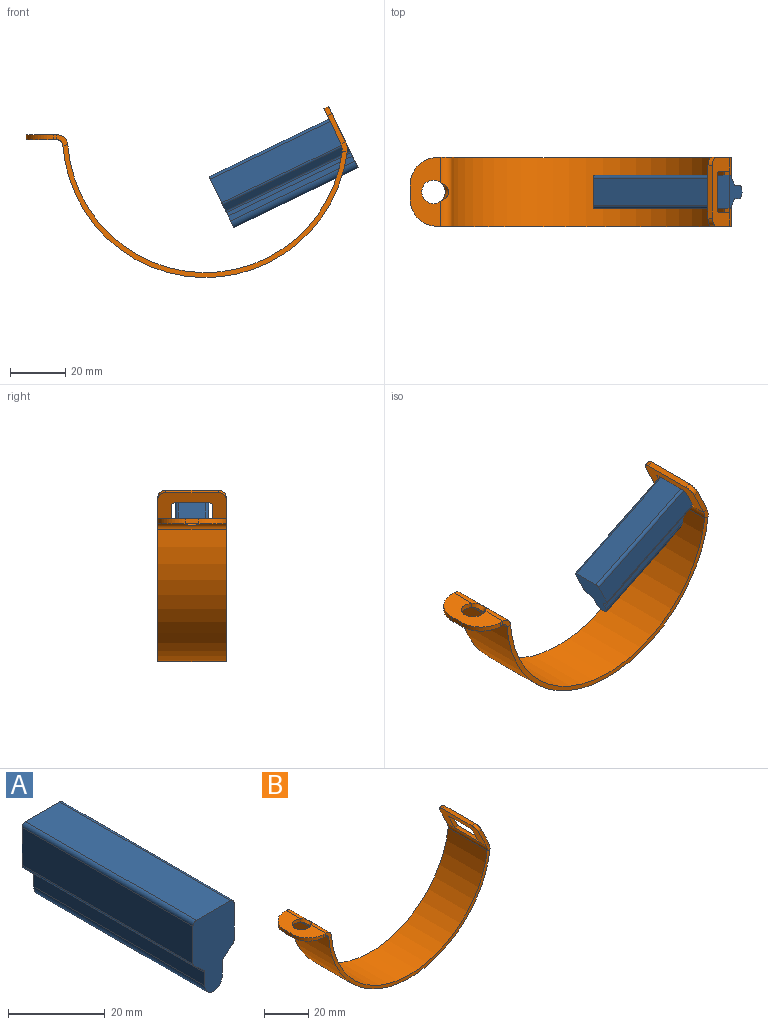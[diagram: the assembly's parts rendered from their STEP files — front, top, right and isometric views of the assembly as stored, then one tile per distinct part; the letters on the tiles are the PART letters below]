
ASSEMBLY  parts=2 mates=1
PART A: 17 faces, bbox 12x50x20.5 mm
  f0: plane 50x2.81mm, normal (-0.65,0,-0.76), area 184.7mm2, adj f9,f10,f11,f16
  f1: plane 50x3.34mm, normal (-1,0,0), area 167.1mm2, adj f2,f9,f10,f11
  f2: cylinder r=2.5mm len=50mm, axis (0,1,0), area 409.1mm2, adj f1,f3,f9,f10
  f3: plane 50x2.09mm, normal (1,0,0), area 104.6mm2, adj f2,f4,f9,f10
  f4: plane 50x1.32mm, normal (1,0,0), area 65.8mm2, adj f3,f9,f10,f12
  f5: plane 50x2.81mm, normal (0.65,0,-0.76), area 184.6mm2, adj f9,f10,f12,f13
  f6: plane 50x9.54mm, normal (1,0,0), area 477mm2, adj f9,f10,f13,f14
  f7: plane 50x10mm, normal (0,0,1), area 500mm2, adj f9,f10,f14,f15
  f8: plane 50x9.54mm, normal (-1,0,0), area 477mm2, adj f9,f10,f15,f16
  f9: plane 20.5x12mm, normal (0,-1,0), area 186.8mm2, adj f0,f1,f2,f3,f4,f5,f6,f7
  f10: plane 20.5x12mm, normal (0,1,0), area 186.8mm2, adj f0,f1,f2,f3,f4,f5,f6,f7
  f11: cylinder r=1mm len=50mm, axis (0,-1,0), area 43.2mm2, adj f0,f1,f9,f10
  f12: cylinder r=1mm len=50mm, axis (0,-1,0), area 43.2mm2, adj f4,f5,f9,f10
  f13: cylinder r=1mm len=50mm, axis (0,-1,0), area 43.2mm2, adj f5,f6,f9,f10
  f14: cylinder r=1mm len=50mm, axis (0,1,0), area 78.5mm2, adj f6,f7,f9,f10
  f15: cylinder r=1mm len=50mm, axis (0,-1,0), area 78.5mm2, adj f7,f8,f9,f10
  f16: cylinder r=1mm len=50mm, axis (0,-1,0), area 43.2mm2, adj f0,f8,f9,f10
PART B: 34 faces, bbox 116.5x25x62 mm
  f0: plane 1.8x1.15mm, normal (0,-1,0), area 2.1mm2, adj f4,f5,f6,f13
  f1: plane 5x1.8mm, normal (-1,0,0), area 9mm2, adj f4,f5,f6,f7
  f2: plane 1.8x1.15mm, normal (0,1,0), area 2.1mm2, adj f4,f5,f7,f12
  f3: cylinder r=4.25mm len=8.5mm, axis (0,0,-1), area 34.3mm2, adj f4,f5,f14
  f4: plane 25x11.15mm, normal (0,0,-1), area 186.5mm2, adj f0,f1,f2,f3,f6,f7,f15
  f5: plane 25x11.15mm, normal (0,0,1), area 186.5mm2, adj f0,f1,f2,f3,f6,f7,f16
  f6: cylinder r=10mm len=10mm, axis (0,0,-1), area 28.3mm2, adj f0,f1,f4,f5
  f7: cylinder r=10mm len=10mm, axis (0,0,1), area 28.3mm2, adj f1,f2,f4,f5
  f8: plane 103.07x48.1mm, normal (0,1,0), area 269.8mm2, adj f10,f11,f12,f29
  f9: plane 103.07x48.1mm, normal (0,-1,0), area 269.8mm2, adj f10,f11,f13,f31
  f10: cylinder r=51.8mm len=103.07mm, axis (0,-1,0), area 3813.8mm2, adj f8,f9,f15,f32
  f11: cylinder r=50mm len=99.49mm, axis (0,-1,0), area 3681.3mm2, adj f8,f9,f16,f33
  f12: plane 3.99x3.84mm, normal (0,1,0), area 8.4mm2, adj f2,f8,f15,f16
  f13: plane 3.99x3.84mm, normal (0,-1,0), area 8.4mm2, adj f0,f9,f15,f16
  f14: bspline ~6.65x2.91mm, area 15.7mm2, adj f3,f15,f16
  f15: cylinder r=2.2mm len=25mm, axis (0,-1,0), area 74.3mm2, adj f4,f10,f12,f13,f14
  f16: cylinder r=4mm len=25mm, axis (0,-1,0), area 135.1mm2, adj f5,f11,f12,f13,f14
  f17: plane 8.89x5.53mm, normal (0,-1,0), area 16.2mm2, adj f23,f24,f27,f30
  f18: plane 10.85x6.47mm, normal (0,1,0), area 20.1mm2, adj f23,f24,f26,f29
  f19: plane 19x1.62mm, normal (-0.43,0,0.9), area 34.2mm2, adj f23,f24,f25,f26
  f20: plane 10.85x6.47mm, normal (0,-1,0), area 20.1mm2, adj f23,f24,f25,f31
  f21: plane 8.89x5.53mm, normal (0,1,0), area 16.2mm2, adj f23,f24,f28,f30
  f22: plane 13x1.62mm, normal (0.43,0,-0.9), area 23.4mm2, adj f23,f24,f27,f28
  f23: plane 25x12.77mm, normal (0.9,0,0.43), area 200.9mm2, adj f17,f18,f19,f20,f21,f22,f25,f26
  f24: plane 25x12.77mm, normal (-0.9,0,-0.43), area 200.9mm2, adj f17,f18,f19,f20,f21,f22,f25,f26
  f25: cylinder r=3mm len=3.48mm, axis (0.9,0,0.43), area 8.5mm2, adj f19,f20,f23,f24
  f26: cylinder r=3mm len=3.48mm, axis (-0.9,0,-0.43), area 8.5mm2, adj f18,f19,f23,f24
  f27: cylinder r=1mm len=2.06mm, axis (-0.9,0,-0.43), area 2.8mm2, adj f17,f22,f23,f24
  f28: cylinder r=1mm len=2.06mm, axis (0.9,0,0.43), area 2.8mm2, adj f21,f22,f23,f24
  f29: plane 3.78x2.3mm, normal (0,1,0), area 6.1mm2, adj f8,f18,f32,f33
  f30: plane 15x1.62mm, normal (-0.43,0,0.9), area 27mm2, adj f17,f21,f32,f33
  f31: plane 3.78x2.3mm, normal (0,-1,0), area 6.1mm2, adj f9,f20,f32,f33
  f32: cylinder r=6.8mm len=25mm, axis (0,-1,0), area 97.2mm2, adj f10,f23,f29,f30,f31
  f33: cylinder r=5mm len=25mm, axis (0,-1,0), area 71.4mm2, adj f11,f24,f29,f30,f31
PLACE A rot(axis=(0.22,-0.22,-0.95),92.8deg) t=(45.71,-17.44,1.82)mm
PLACE B t=(-5.85,-4.94,-8.77)mm
MATE fastened A.f7 <-> B.f22  axis (-0.43,0,0.9) through (40.93,-17.44,11.73)mm
